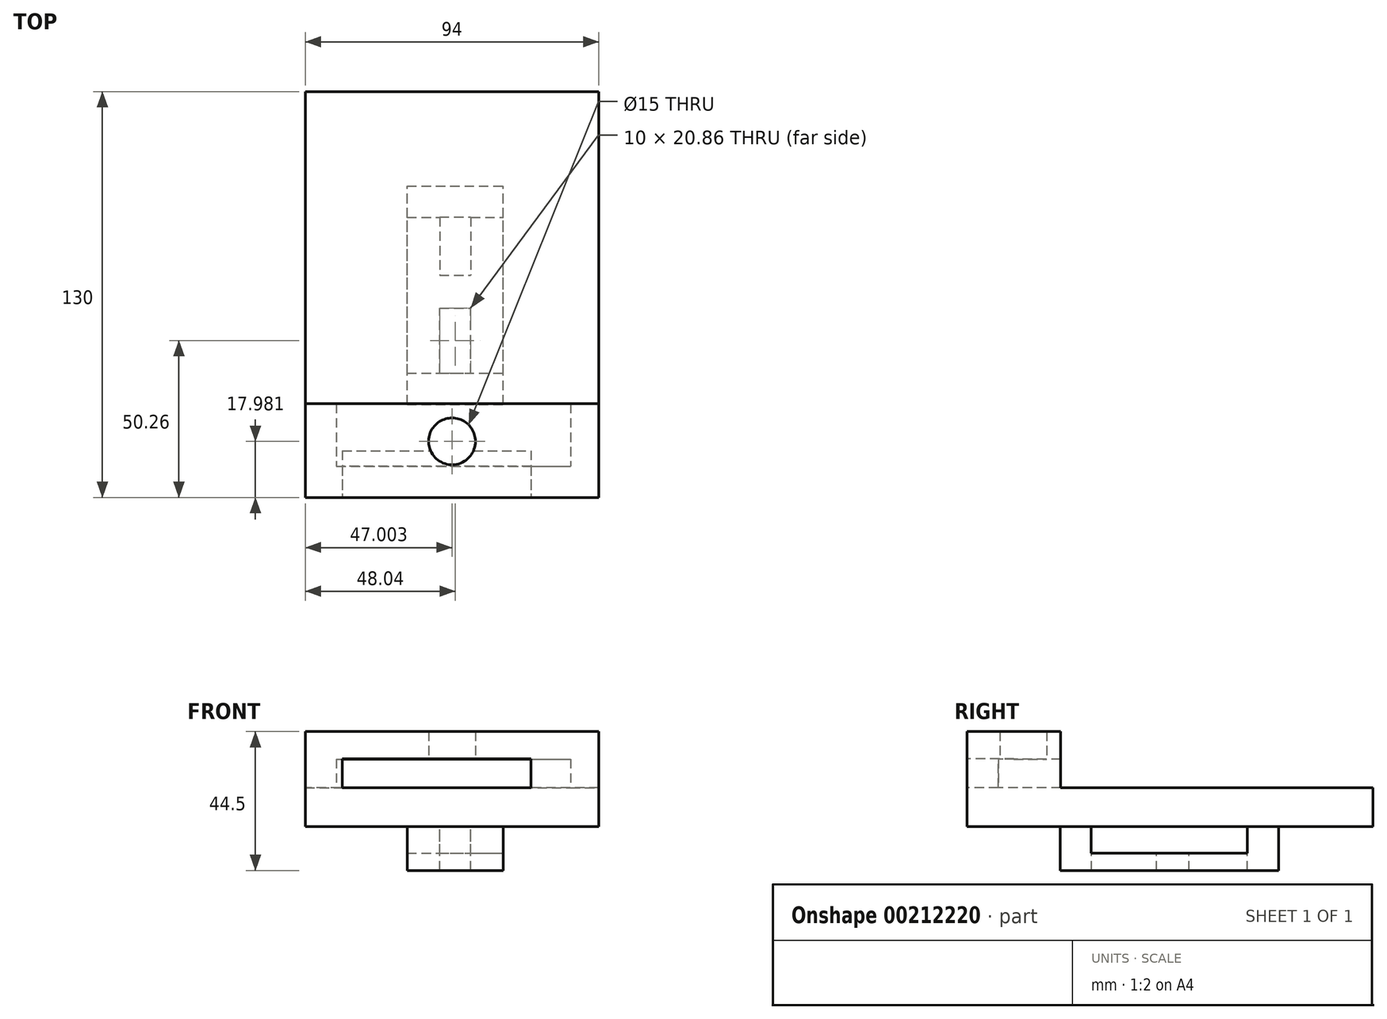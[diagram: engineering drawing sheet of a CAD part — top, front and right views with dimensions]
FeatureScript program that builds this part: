
annotation { "Feature Type Name" : "Feature", "Feature Type Description" : "" }
export const myFeature = defineFeature(function(context is Context, id is Id, definition is map)
    precondition{}
    {
        {
            var Q0;
            Q0=qCreatedBy(makeId("Top.planeOp"),FACE);
            var sketch = newSketch(context, id + "F0", { "sketchPlane" : qUnion([Q0])});
            skLineSegment(sketch, "E0.bottom", {"start": v(-33.04, -18.8) * mm, "end": v(41.96, -18.8) * mm});
            skLineSegment(sketch, "E0.top", {"start": v(-33.04, -38.8) * mm, "end": v(41.96, -38.8) * mm});
            skLineSegment(sketch, "E0.left", {"start": v(-33.04, -18.8) * mm, "end": v(-33.04, -38.8) * mm});
            skLineSegment(sketch, "E0.right", {"start": v(41.96, -18.8) * mm, "end": v(41.96, -38.8) * mm});
            skSolve(sketch);
        }
        {
            var Q0;
            Q0=qCreatedBy(makeId("Top.planeOp"),FACE);
            var sketch = newSketch(context, id + "F1", { "sketchPlane" : qUnion([Q0])});
            skLineSegment(sketch, "E1.0", {"start": v(-43.04, 81.2) * mm, "end": v(-43.04, -48.8) * mm});
            skLineSegment(sketch, "E1.1", {"start": v(50.96, 81.2) * mm, "end": v(-43.04, 81.2) * mm});
            skLineSegment(sketch, "E1.2", {"start": v(50.96, -48.8) * mm, "end": v(50.96, 81.2) * mm});
            skLineSegment(sketch, "E1.3", {"start": v(-43.04, -48.8) * mm, "end": v(50.96, -48.8) * mm});
            skLineSegment(sketch, "E2.right", {"start": v(-43.04, 11.1) * mm, "end": v(-43.04, 16.2) * mm});
            skSolve(sketch);
        }
        {
            var Q0;
            Q0=makeQuery(id+"F1.imprint","IMPRINT",FACE,{"disambiguationData":[TD([[makeQuery(id+"F1.imprint","IMPRINT",EDGE,{"derivedFrom":sQuery(id+"F1.wireOp",EDGE,"E1.0")}),1.0]])]});
            extrude(context, id + "F2", {"entities" : qUnion([Q0]), "oppositeDirection" : true, "depth" : 12.5 * mm});
        }
        {
            var Q0;
            Q0=makeQuery(id+"F2.opExtrude","CAP_FACE",FACE,{"disambiguationData":[OSD([sQuery(id+"F1.wireOp",EDGE,"u7t7iiTI-UsOk-mcI5-G1dA-rIgg98Dc1Poo.bottom"),sQuery(id+"F1.wireOp",EDGE,"u7t7iiTI-UsOk-mcI5-G1dA-rIgg98Dc1Poo.top"),sQuery(id+"F1.wireOp",EDGE,"u7t7iiTI-UsOk-mcI5-G1dA-rIgg98Dc1Poo.left"),sQuery(id+"F1.wireOp",EDGE,"u7t7iiTI-UsOk-mcI5-G1dA-rIgg98Dc1Poo.right"),sQuery(id+"F1.wireOp",EDGE,"E1.0"),sQuery(id+"F1.wireOp",EDGE,"E1.1"),sQuery(id+"F1.wireOp",EDGE,"E1.2"),sQuery(id+"F1.wireOp",EDGE,"E1.3")])],"isStart":true});
            var sketch = newSketch(context, id + "F3", { "sketchPlane" : qUnion([Q0])});
            skLineSegment(sketch, "E3.bottom", {"start": v(-43.04, -48.8) * mm, "end": v(50.96, -48.8) * mm});
            skLineSegment(sketch, "E3.top", {"start": v(-43.04, -18.8) * mm, "end": v(50.96, -18.8) * mm});
            skLineSegment(sketch, "E3.left", {"start": v(-43.04, -48.8) * mm, "end": v(-43.04, -18.8) * mm});
            skLineSegment(sketch, "E3.right", {"start": v(50.96, -48.8) * mm, "end": v(50.96, -18.8) * mm});
            skCircle(sketch, "E4", {"center": v(3.96, -30.82) * mm, "radius": 7.5 * mm});
            skSolve(sketch);
        }
        {
            var Q0;
            Q0 = qSketchRegion(id + "F3", true);
            extrude(context, id + "F4", {"entities" : qUnion([Q0]), "operationType" : NewBodyOperationType.ADD, "depth" : 18 * mm});
        }
        {
            var Q0;
            Q0 = qSketchRegion(id + "F0", true);
            extrude(context, id + "F5", {"entities" : qUnion([Q0]), "operationType" : NewBodyOperationType.REMOVE, "depth" : 9.2 * mm});
        }
        {
            var Q0;
            Q0=makeQuery(id+"F2.opExtrude","CAP_FACE",FACE,{"disambiguationData":[OSD([sQuery(id+"F1.wireOp",EDGE,"E1.0"),sQuery(id+"F1.wireOp",EDGE,"E1.1"),sQuery(id+"F1.wireOp",EDGE,"E1.2"),sQuery(id+"F1.wireOp",EDGE,"E1.3"),sQuery(id+"F1.wireOp",EDGE,"E2.right")])],"isStart":false});
            var sketch = newSketch(context, id + "F6", { "sketchPlane" : qUnion([Q0])});
            skLineSegment(sketch, "E5.bottom", {"start": v(-10.4, 18.97) * mm, "end": v(20.4, 18.97) * mm});
            skLineSegment(sketch, "E5.top", {"start": v(-10.4, -51.03) * mm, "end": v(20.4, -51.03) * mm});
            skLineSegment(sketch, "E5.left", {"start": v(-10.4, 18.97) * mm, "end": v(-10.4, -51.03) * mm});
            skLineSegment(sketch, "E5.right", {"start": v(20.4, 18.97) * mm, "end": v(20.4, -51.03) * mm});
            skLineSegment(sketch, "E6", {"start": v(5, -41.03) * mm, "end": v(10, -41.03) * mm});
            skLineSegment(sketch, "E7", {"start": v(5, 8.97) * mm, "end": v(10, 8.97) * mm});
            skLineSegment(sketch, "E8", {"start": v(5, -41.03) * mm, "end": v(0, -41.03) * mm});
            skLineSegment(sketch, "E9", {"start": v(5, 8.97) * mm, "end": v(0, 8.97) * mm});
            skLineSegment(sketch, "E10", {"start": v(0, -11.89) * mm, "end": v(10, -11.89) * mm});
            skLineSegment(sketch, "E11", {"start": v(0, -22.37) * mm, "end": v(10, -22.37) * mm});
            skLineSegment(sketch, "E12", {"start": v(10, 8.97) * mm, "end": v(10, -11.89) * mm});
            skLineSegment(sketch, "E13", {"start": v(0, 8.97) * mm, "end": v(0, -11.89) * mm});
            skLineSegment(sketch, "E14", {"start": v(10, -41.03) * mm, "end": v(10, -22.37) * mm});
            skLineSegment(sketch, "E15", {"start": v(0, -41.03) * mm, "end": v(0, -22.37) * mm});
            skSolve(sketch);
        }
        {
            var Q0;
            Q0 = qSketchRegion(id + "F6", true);
            extrude(context, id + "F7", {"entities" : qUnion([Q0]), "operationType" : NewBodyOperationType.ADD, "depth" : 14 * mm});
        }
        {
            var Q0;
            {var subQ0=sQuery(id+"F1.wireOp",EDGE,"E2.right");var subQ1=sQuery(id+"F1.wireOp",EDGE,"E1.0");var subQ2=sQuery(id+"F1.wireOp",EDGE,"E1.1");var subQ3=sQuery(id+"F1.wireOp",EDGE,"E1.2");var subQ4=sQuery(id+"F1.wireOp",EDGE,"E1.3");Q0=makeQuery(id+"F7.boolean.opBoolean","SPLIT",FACE,{"disambiguationData":[TD([makeQuery(id+"F2.opExtrude","SWEPT_FACE",FACE,{"disambiguationData":[OSD([subQ2])]})])],"derivedFrom":makeQuery(id+"F2.opExtrude","CAP_FACE",FACE,{"disambiguationData":[OSD([subQ1,subQ2,subQ3,subQ4,subQ0])],"isStart":false})});}
            var sketch = newSketch(context, id + "F8", { "sketchPlane" : qUnion([Q0])});
            skLineSegment(sketch, "E16.bottom", {"start": v(-14.6, 9.01) * mm, "end": v(20.4, 9.01) * mm});
            skLineSegment(sketch, "E16.top", {"start": v(-14.6, -41) * mm, "end": v(20.4, -41) * mm});
            skLineSegment(sketch, "E16.left", {"start": v(-14.6, 9.01) * mm, "end": v(-14.6, -41) * mm});
            skLineSegment(sketch, "E16.right", {"start": v(20.4, 9.01) * mm, "end": v(20.4, -41) * mm});
            skSolve(sketch);
        }
        {
            var Q0;
            Q0 = qSketchRegion(id + "F8", true);
            var Q1;
            Q1=sQuery(id+"F8.wireOp",EDGE,"E16.left");
            extrude(context, id + "F9", {"entities" : qUnion([Q0]), "operationType" : NewBodyOperationType.REMOVE, "surfaceEntities" : qUnion([Q1]), "depth" : 8.5 * mm});
        }
        {
            var Q0;
            Q0=makeQuery(id+"F4.boolean.opBoolean","MERGE",FACE,{"derivedFrom":[makeQuery(id+"F2.opExtrude","SWEPT_FACE",FACE,{"disambiguationData":[OSD([sQuery(id+"F1.wireOp",EDGE,"E1.3")])]}),makeQuery(id+"F4.opExtrude","SWEPT_FACE",FACE,{"disambiguationData":[OSD([sQuery(id+"F3.wireOp",EDGE,"E3.bottom")])]})]});
            var sketch = newSketch(context, id + "F10", { "sketchPlane" : qUnion([Q0])});
            skLineSegment(sketch, "E17.bottom", {"start": v(-31.2, 9.3) * mm, "end": v(29.32, 9.3) * mm});
            skLineSegment(sketch, "E17.top", {"start": v(-31.2, 0.06) * mm, "end": v(29.32, 0.06) * mm});
            skLineSegment(sketch, "E17.left", {"start": v(-31.2, 9.3) * mm, "end": v(-31.2, 0.06) * mm});
            skLineSegment(sketch, "E17.right", {"start": v(29.32, 9.3) * mm, "end": v(29.32, 0.06) * mm});
            skSolve(sketch);
        }
        {
            var Q0;
            Q0=makeQuery(id+"F10.imprint","IMPRINT",FACE,{"disambiguationData":[TD([[makeQuery(id+"F10.imprint","IMPRINT",EDGE,{"derivedFrom":sQuery(id+"F10.wireOp",EDGE,"E17.bottom")}),-1.0]])]});
            extrude(context, id + "F11", {"entities" : qUnion([Q0]), "operationType" : NewBodyOperationType.REMOVE, "oppositeDirection" : true, "depth" : 15 * mm});
        }
    });
